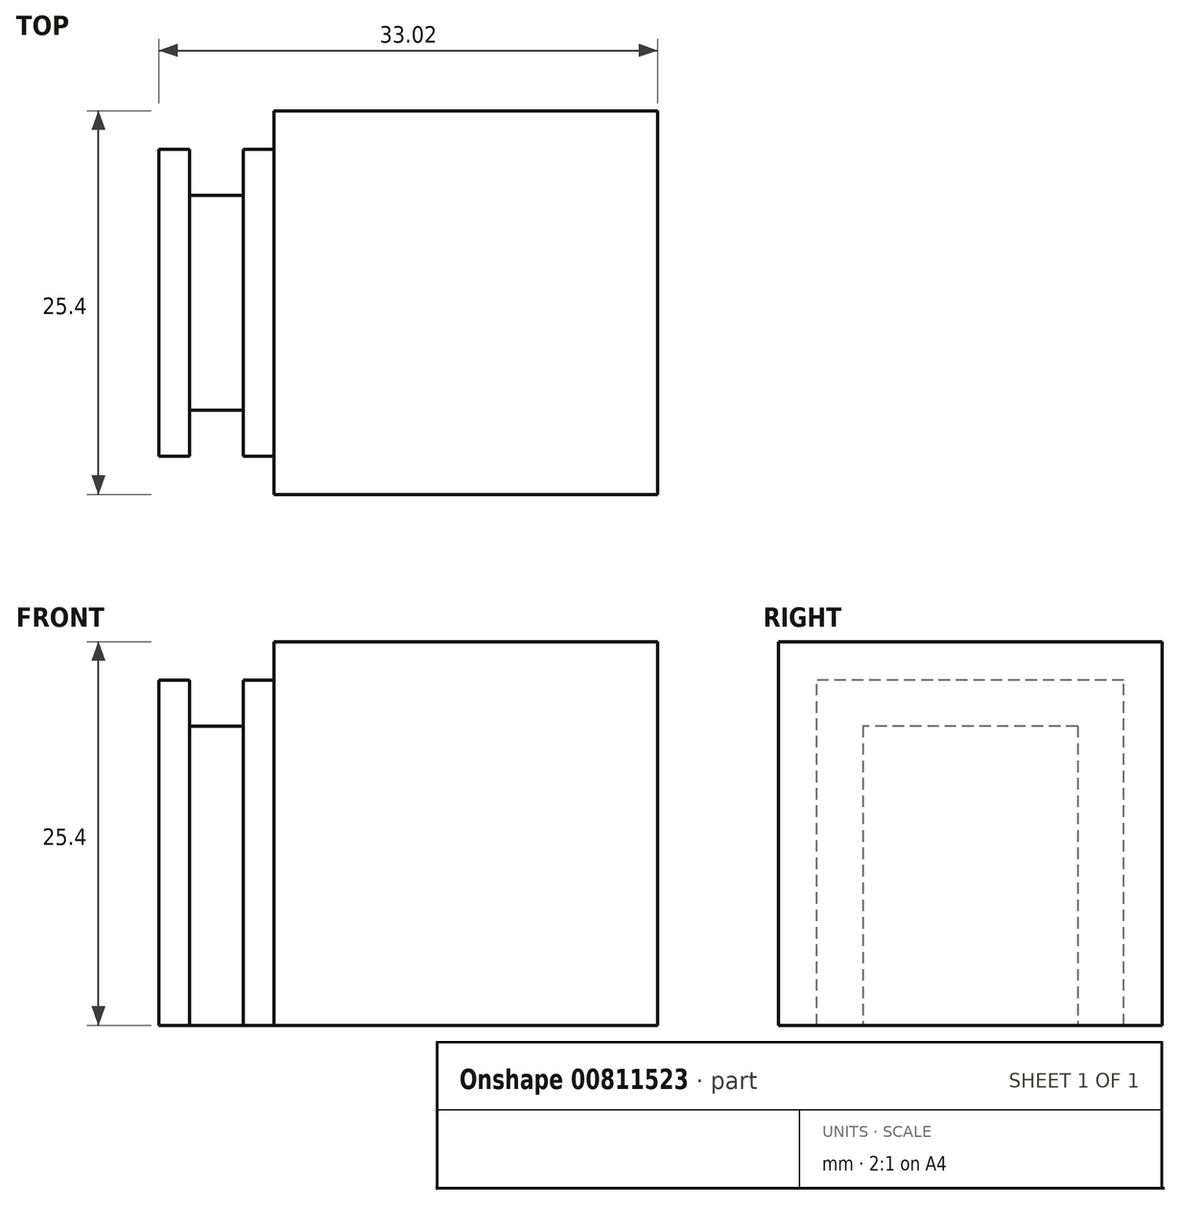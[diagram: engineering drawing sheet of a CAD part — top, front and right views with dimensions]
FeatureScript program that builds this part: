
annotation { "Feature Type Name" : "Feature", "Feature Type Description" : "" }
export const myFeature = defineFeature(function(context is Context, id is Id, definition is map)
    precondition{}
    {
        {
            var Q0;
            Q0=qCreatedBy(makeId("Top.planeOp"),FACE);
            var sketch = newSketch(context, id + "F0", { "sketchPlane" : qUnion([Q0])});
            skLineSegment(sketch, "E0.bottom", {"start": v(12.7, -12.7) * mm, "end": v(-12.7, -12.7) * mm});
            skLineSegment(sketch, "E0.top", {"start": v(12.7, 12.7) * mm, "end": v(-12.7, 12.7) * mm});
            skLineSegment(sketch, "E0.left", {"start": v(12.7, -12.7) * mm, "end": v(12.7, 12.7) * mm});
            skLineSegment(sketch, "E0.right", {"start": v(-12.7, -12.7) * mm, "end": v(-12.7, 12.7) * mm});
            skPoint(sketch, "E0.middle", {"position": v(0, 0) * mm});
            skSolve(sketch);
        }
        {
            var Q0;
            Q0=makeQuery(id+"F0.imprint","IMPRINT",FACE,{"disambiguationData":[TD([[makeQuery(id+"F0.imprint","IMPRINT",EDGE,{"derivedFrom":sQuery(id+"F0.wireOp",EDGE,"E0.bottom")}),-1.0]])]});
            extrude(context, id + "F1", {"entities" : qUnion([Q0]), "depth" : 25.4 * mm, "offsetDistance" : 25.4 * mm});
        }
        {
            var Q0;
            Q0=makeQuery(id+"F1.opExtrude","SWEPT_FACE",FACE,{"disambiguationData":[OSD([sQuery(id+"F0.wireOp",EDGE,"E0.right")])]});
            var sketch = newSketch(context, id + "F2", { "sketchPlane" : qUnion([Q0])});
            skLineSegment(sketch, "E1", {"start": v(-12.7, 0) * mm, "end": v(-10.16, 0) * mm});
            skLineSegment(sketch, "E2", {"start": v(-10.16, 0) * mm, "end": v(-10.16, 22.86) * mm});
            skLineSegment(sketch, "E3", {"start": v(-10.16, 22.86) * mm, "end": v(10.16, 22.86) * mm});
            skLineSegment(sketch, "E4", {"start": v(10.16, 22.86) * mm, "end": v(10.16, 0) * mm});
            skLineSegment(sketch, "E5", {"start": v(10.16, 0) * mm, "end": v(12.7, 0) * mm});
            skSolve(sketch);
        }
        {
            var Q0;
            {var subQ0=sQuery(id+"F2.wireOp",EDGE,"E2");Q0=makeQuery(id+"F2.imprint","IMPRINT",FACE,{"disambiguationData":[TD([[makeQuery(id+"F2.imprint","IMPRINT",EDGE,{"derivedFrom":subQ0}),-1.0]])]});}
            extrude(context, id + "F3", {"entities" : qUnion([Q0]), "operationType" : NewBodyOperationType.ADD, "depth" : 7.62 * mm, "offsetDistance" : 25.4 * mm});
        }
        {
            var Q0;
            Q0=makeQuery(id+"F3.opExtrude","SWEPT_FACE",FACE,{"disambiguationData":[OSD([sQuery(id+"F2.wireOp",EDGE,"E3")])]});
            var sketch = newSketch(context, id + "F4", { "sketchPlane" : qUnion([Q0])});
            skLineSegment(sketch, "E6", {"start": v(-20.32, 10.16) * mm, "end": v(-18.29, 10.16) * mm});
            skLineSegment(sketch, "E7.bottom", {"start": v(-18.29, 10.16) * mm, "end": v(-14.73, 10.16) * mm});
            skLineSegment(sketch, "E7.top", {"start": v(-18.29, -10.16) * mm, "end": v(-14.73, -10.16) * mm});
            skLineSegment(sketch, "E7.left", {"start": v(-18.29, 10.16) * mm, "end": v(-18.29, -10.16) * mm});
            skLineSegment(sketch, "E7.right", {"start": v(-14.73, 10.16) * mm, "end": v(-14.73, -10.16) * mm});
            skSolve(sketch);
        }
        {
            var Q0;
            Q0=makeQuery(id+"F4.imprint","IMPRINT",FACE,{"disambiguationData":[TD([[makeQuery(id+"F4.imprint","IMPRINT",EDGE,{"derivedFrom":sQuery(id+"F4.wireOp",EDGE,"E7.bottom")}),-1.0]])]});
            extrude(context, id + "F5", {"entities" : qUnion([Q0]), "operationType" : NewBodyOperationType.REMOVE, "oppositeDirection" : true, "depth" : 3.05 * mm, "offsetDistance" : 25.4 * mm});
        }
        {
            var Q0;
            Q0=makeQuery(id+"F3.opExtrude","SWEPT_FACE",FACE,{"disambiguationData":[OSD([sQuery(id+"F2.wireOp",EDGE,"E4")])]});
            var sketch = newSketch(context, id + "F6", { "sketchPlane" : qUnion([Q0])});
            skLineSegment(sketch, "E8.bottom", {"start": v(-18.29, 19.81) * mm, "end": v(-14.73, 19.81) * mm});
            skLineSegment(sketch, "E8.top", {"start": v(-18.29, 0) * mm, "end": v(-14.73, 0) * mm});
            skLineSegment(sketch, "E8.left", {"start": v(-18.29, 19.81) * mm, "end": v(-18.29, 0) * mm});
            skLineSegment(sketch, "E8.right", {"start": v(-14.73, 19.81) * mm, "end": v(-14.73, 0) * mm});
            skSolve(sketch);
        }
        {
            var Q0;
            Q0=makeQuery(id+"F6.imprint","IMPRINT",FACE,{"disambiguationData":[TD([[makeQuery(id+"F6.imprint","IMPRINT",EDGE,{"derivedFrom":sQuery(id+"F6.wireOp",EDGE,"E8.bottom")}),-1.0]])]});
            extrude(context, id + "F7", {"entities" : qUnion([Q0]), "operationType" : NewBodyOperationType.REMOVE, "oppositeDirection" : true, "depth" : 3.05 * mm, "offsetDistance" : 25.4 * mm});
        }
        {
            var Q0;
            Q0=makeQuery(id+"F3.opExtrude","SWEPT_FACE",FACE,{"disambiguationData":[OSD([sQuery(id+"F2.wireOp",EDGE,"E2")])]});
            var sketch = newSketch(context, id + "F8", { "sketchPlane" : qUnion([Q0])});
            skLineSegment(sketch, "E9.bottom", {"start": v(14.73, 19.81) * mm, "end": v(18.29, 19.81) * mm});
            skLineSegment(sketch, "E9.top", {"start": v(14.73, 0) * mm, "end": v(18.29, 0) * mm});
            skLineSegment(sketch, "E9.left", {"start": v(14.73, 19.81) * mm, "end": v(14.73, 0) * mm});
            skLineSegment(sketch, "E9.right", {"start": v(18.29, 19.81) * mm, "end": v(18.29, 0) * mm});
            skSolve(sketch);
        }
        {
            var Q0;
            Q0=makeQuery(id+"F8.imprint","IMPRINT",FACE,{"disambiguationData":[TD([[makeQuery(id+"F8.imprint","IMPRINT",EDGE,{"derivedFrom":sQuery(id+"F8.wireOp",EDGE,"E9.bottom")}),1.0]])]});
            extrude(context, id + "F9", {"entities" : qUnion([Q0]), "operationType" : NewBodyOperationType.REMOVE, "oppositeDirection" : true, "depth" : 3.05 * mm, "offsetDistance" : 25.4 * mm});
        }
        {
            var Q0;
            Q0=makeQuery(id+"F1.opExtrude","SWEPT_BODY",BODY,{"disambiguationData":[OSD([sQuery(id+"F0.wireOp",EDGE,"E0.bottom"),sQuery(id+"F0.wireOp",EDGE,"E0.top"),sQuery(id+"F0.wireOp",EDGE,"E0.left"),sQuery(id+"F0.wireOp",EDGE,"E0.right")])]});
            transform(context, id + "F10", {"entities" : qUnion([Q0]), "transformType" : TransformType.TRANSLATION_3D, "dx" : -54.1 * mm, "dy" : 0 * mm, "dz" : 0 * mm, "makeCopy" : true});
        }
        {
            var Q0;
            Q0=makeQuery(id+"F10.opPattern","COPY",BODY,{"derivedFrom":makeQuery(id+"F1.opExtrude","SWEPT_BODY",BODY,{"disambiguationData":[OSD([sQuery(id+"F0.wireOp",EDGE,"E0.bottom"),sQuery(id+"F0.wireOp",EDGE,"E0.top"),sQuery(id+"F0.wireOp",EDGE,"E0.left"),sQuery(id+"F0.wireOp",EDGE,"E0.right")])]}),"instanceName":"1"});
            deleteBodies(context, id + "F11", {"entities" : qUnion([Q0])});
        }
    });
